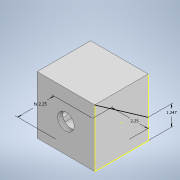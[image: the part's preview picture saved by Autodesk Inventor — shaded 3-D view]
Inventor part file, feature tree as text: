
AUTODESK INVENTOR PART (.ipt)
format: ipt  version: 2022.2 (Build 262287030, 287C)  size: 128,000 bytes
history: native  units: in
note: dims shown in document units (in); Inventor stores cm internally (conversion verified against a paired STEP export)
features: sketch x6, extrude x4
ambient origin geometry x8: Origin, YZ Plane, XZ Plane, XY Plane, X Axis, Y Axis, Z Axis, Center Point
bodies: Solid1 (feature_tree)
feature tree (10):
  extrude  "Extrusion1"  Depth=1.4in
  sketch  "Sketch2"  dims[d2=1.2992in d3=0.0in d4=0.8858in]
  sketch  "Sketch3"  dims[d5=0.8858in d6=0.491in]
  extrude  "Extrusion2"  Depth=1.2992in
  extrude  "Extrusion3"  Depth=0.491in
  extrude  "Extrusion4"  Depth=1.2425in
  sketch  "Sketch1"  dims[d0=1.4in d1=1.4in]
  sketch  "Sketch4"  dims[d7=1.2425in d8=1.2425in]
  sketch  "Sketch5"  dims[d9=1.1811in d10=0.0in]
  sketch  "Sketch6"  dims[d11=0.3984in d12=0.0in d13=0.0in d14=0.2598in d16=0.0787in d17=0.0in d18=0.6in d19=0.0344in]
